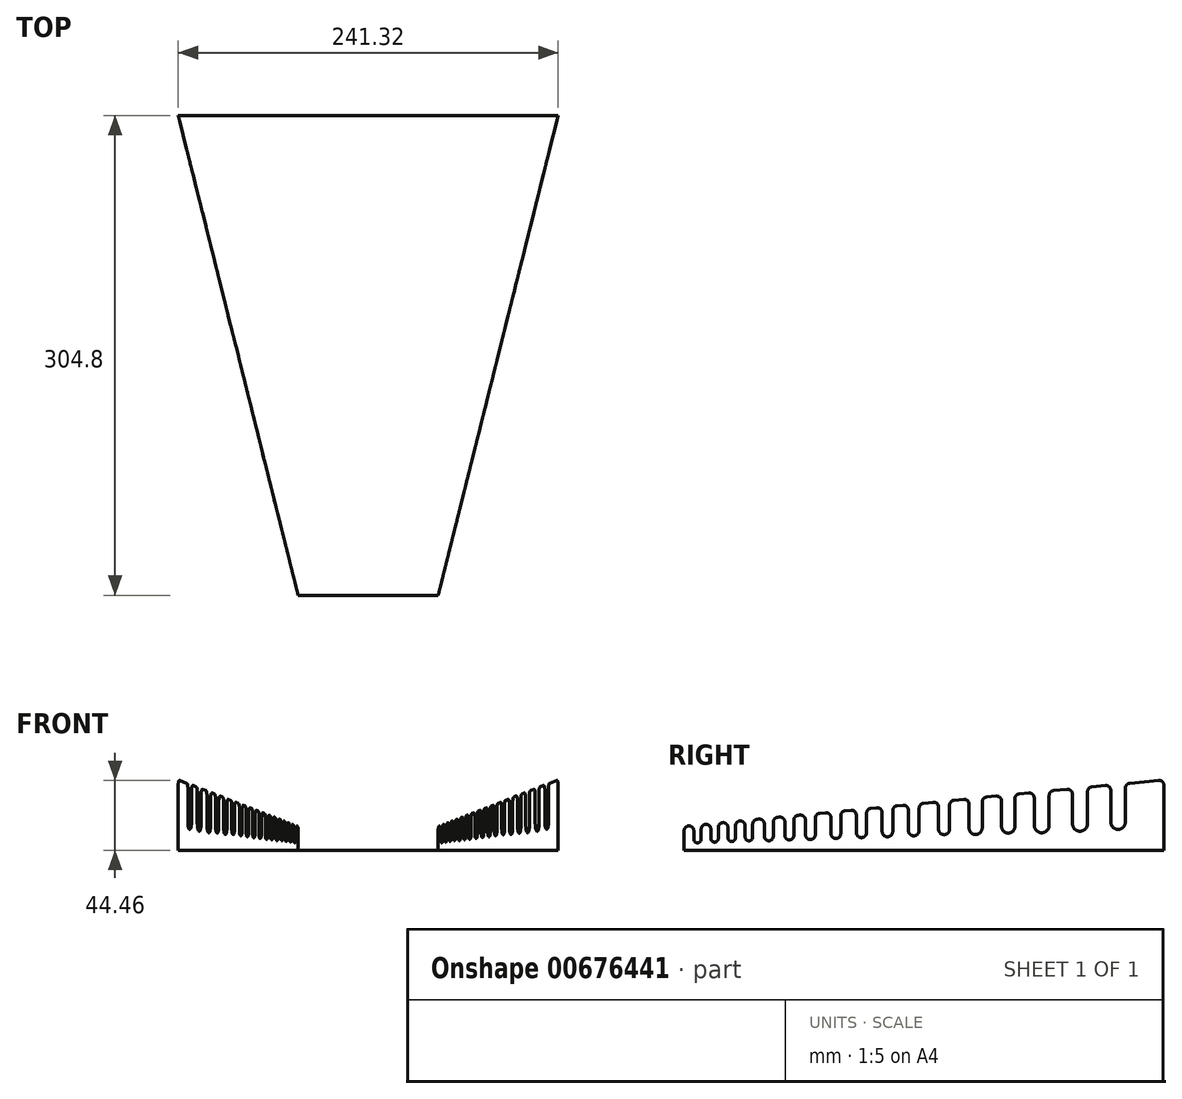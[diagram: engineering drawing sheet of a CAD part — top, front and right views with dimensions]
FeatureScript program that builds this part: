
annotation { "Feature Type Name" : "Feature", "Feature Type Description" : "" }
export const myFeature = defineFeature(function(context is Context, id is Id, definition is map)
    precondition{}
    {
        {
            var Q0;
            Q0=qCreatedBy(makeId("Top.planeOp"),FACE);
            var sketch = newSketch(context, id + "F0", { "sketchPlane" : qUnion([Q0])});
            skLineSegment(sketch, "E0", {"start": v(-44.45, 0) * mm, "end": v(44.45, 0) * mm});
            skLineSegment(sketch, "E1", {"start": v(44.45, 0) * mm, "end": v(120.65, 304.8) * mm});
            skLineSegment(sketch, "E2", {"start": v(120.65, 304.8) * mm, "end": v(-120.65, 304.8) * mm});
            skLineSegment(sketch, "E3", {"start": v(-120.65, 304.8) * mm, "end": v(-44.45, 0) * mm});
            skSolve(sketch);
        }
        {
            var Q0;
            Q0=qSketchRegion(id+"F0",true);
            extrude(context, id + "F1", {"entities" : qUnion([Q0]), "depth" : 3 / 406.4 * mm});
        }
        {
            var Q0;
            Q0=makeQuery(id+"F1.opExtrude","SWEPT_FACE",FACE,{"disambiguationData":[OSD([sQuery(id+"F0.wireOp",EDGE,"E1")])]});
            var sketch = newSketch(context, id + "F2", { "sketchPlane" : qUnion([Q0])});
            skLineSegment(sketch, "E4", {"start": v(10.78, 0) * mm, "end": v(10.78, 12.35) * mm});
            skLineSegment(sketch, "E5", {"start": v(13.66, 15.51) * mm, "end": v(13.66, 15.51) * mm});
            skLineSegment(sketch, "E6", {"start": v(17.13, 12.35) * mm, "end": v(17.13, 7.18) * mm});
            skLineSegment(sketch, "E7", {"start": v(17.13, 7.18) * mm, "end": v(21.96, 7.37) * mm, "construction": true});
            skLineSegment(sketch, "E8", {"start": v(21.96, 7.37) * mm, "end": v(21.96, 13.4) * mm});
            skLineSegment(sketch, "E9", {"start": v(24.83, 16.56) * mm, "end": v(24.83, 16.56) * mm});
            skLineSegment(sketch, "E10", {"start": v(28.3, 13.4) * mm, "end": v(28.3, 7.62) * mm});
            skLineSegment(sketch, "E11", {"start": v(28.3, 7.62) * mm, "end": v(33.13, 7.82) * mm, "construction": true});
            skLineSegment(sketch, "E12", {"start": v(33.13, 7.82) * mm, "end": v(33.13, 14.45) * mm});
            skLineSegment(sketch, "E13", {"start": v(36.01, 17.61) * mm, "end": v(36.01, 17.61) * mm});
            skLineSegment(sketch, "E14", {"start": v(39.48, 14.45) * mm, "end": v(39.48, 8.07) * mm});
            skLineSegment(sketch, "E15", {"start": v(39.48, 8.07) * mm, "end": v(44.38, 8.27) * mm, "construction": true});
            skLineSegment(sketch, "E16", {"start": v(44.38, 8.27) * mm, "end": v(44.38, 15.5) * mm});
            skLineSegment(sketch, "E17", {"start": v(47.26, 18.67) * mm, "end": v(47.26, 18.67) * mm});
            skLineSegment(sketch, "E18", {"start": v(50.73, 15.5) * mm, "end": v(50.73, 8.52) * mm});
            skLineSegment(sketch, "E19", {"start": v(50.73, 8.52) * mm, "end": v(55.69, 8.72) * mm, "construction": true});
            skLineSegment(sketch, "E20", {"start": v(55.69, 8.72) * mm, "end": v(55.69, 16.57) * mm});
            skLineSegment(sketch, "E21", {"start": v(58.57, 19.73) * mm, "end": v(59.84, 19.85) * mm});
            skLineSegment(sketch, "E22", {"start": v(63.3, 16.7) * mm, "end": v(63.3, 9.02) * mm});
            skLineSegment(sketch, "E23", {"start": v(63.3, 9.02) * mm, "end": v(69.15, 9.26) * mm, "construction": true});
            skLineSegment(sketch, "E24", {"start": v(69.15, 9.26) * mm, "end": v(69.15, 17.84) * mm});
            skLineSegment(sketch, "E25", {"start": v(72.03, 21) * mm, "end": v(73.3, 21.12) * mm});
            skLineSegment(sketch, "E26", {"start": v(76.77, 17.96) * mm, "end": v(76.77, 9.56) * mm});
            skLineSegment(sketch, "E27", {"start": v(76.77, 9.56) * mm, "end": v(82.61, 9.8) * mm, "construction": true});
            skLineSegment(sketch, "E28", {"start": v(82.61, 9.8) * mm, "end": v(82.61, 19.1) * mm});
            skLineSegment(sketch, "E29", {"start": v(85.49, 22.26) * mm, "end": v(86.76, 22.38) * mm});
            skLineSegment(sketch, "E30", {"start": v(90.23, 19.22) * mm, "end": v(90.23, 10.1) * mm});
            skLineSegment(sketch, "E31", {"start": v(90.23, 10.1) * mm, "end": v(96.7, 10.36) * mm, "construction": true});
            skLineSegment(sketch, "E32", {"start": v(96.7, 10.36) * mm, "end": v(96.7, 20.43) * mm});
            skLineSegment(sketch, "E33", {"start": v(99.59, 23.59) * mm, "end": v(103.4, 23.95) * mm});
            skLineSegment(sketch, "E34", {"start": v(106.87, 20.79) * mm, "end": v(106.87, 10.77) * mm});
            skLineSegment(sketch, "E35", {"start": v(106.87, 10.77) * mm, "end": v(113.35, 11.02) * mm, "construction": true});
            skLineSegment(sketch, "E36", {"start": v(113.35, 11.02) * mm, "end": v(113.35, 22) * mm});
            skLineSegment(sketch, "E37", {"start": v(116.22, 25.15) * mm, "end": v(120.03, 25.51) * mm});
            skLineSegment(sketch, "E38", {"start": v(123.5, 22.35) * mm, "end": v(123.5, 11.43) * mm});
            skLineSegment(sketch, "E39", {"start": v(123.5, 11.43) * mm, "end": v(130.24, 11.7) * mm, "construction": true});
            skLineSegment(sketch, "E40", {"start": v(130.24, 11.7) * mm, "end": v(130.24, 23.58) * mm});
            skLineSegment(sketch, "E41", {"start": v(133.11, 26.74) * mm, "end": v(136.92, 27.1) * mm});
            skLineSegment(sketch, "E42", {"start": v(140.4, 23.94) * mm, "end": v(140.4, 12.1) * mm});
            skLineSegment(sketch, "E43", {"start": v(140.4, 12.1) * mm, "end": v(147.38, 12.39) * mm, "construction": true});
            skLineSegment(sketch, "E44", {"start": v(147.38, 12.39) * mm, "end": v(147.38, 25.2) * mm});
            skLineSegment(sketch, "E45", {"start": v(150.26, 28.35) * mm, "end": v(154.07, 28.71) * mm});
            skLineSegment(sketch, "E46", {"start": v(157.54, 25.55) * mm, "end": v(157.54, 12.8) * mm});
            skLineSegment(sketch, "E47", {"start": v(157.54, 12.8) * mm, "end": v(164.65, 13.08) * mm, "construction": true});
            skLineSegment(sketch, "E48", {"start": v(164.65, 13.08) * mm, "end": v(164.65, 26.82) * mm});
            skLineSegment(sketch, "E49", {"start": v(167.53, 29.98) * mm, "end": v(173.88, 30.57) * mm});
            skLineSegment(sketch, "E50", {"start": v(177.35, 27.41) * mm, "end": v(177.35, 13.59) * mm});
            skLineSegment(sketch, "E51", {"start": v(177.35, 13.59) * mm, "end": v(184.6, 13.88) * mm, "construction": true});
            skLineSegment(sketch, "E52", {"start": v(184.6, 13.88) * mm, "end": v(184.6, 28.69) * mm});
            skLineSegment(sketch, "E53", {"start": v(187.47, 31.85) * mm, "end": v(193.82, 32.45) * mm});
            skLineSegment(sketch, "E54", {"start": v(197.3, 29.29) * mm, "end": v(197.3, 14.38) * mm});
            skLineSegment(sketch, "E55", {"start": v(197.3, 14.38) * mm, "end": v(205.93, 14.73) * mm, "construction": true});
            skLineSegment(sketch, "E56", {"start": v(205.93, 14.73) * mm, "end": v(205.93, 30.7) * mm});
            skLineSegment(sketch, "E57", {"start": v(208.8, 33.86) * mm, "end": v(215.16, 34.45) * mm});
            skLineSegment(sketch, "E58", {"start": v(218.63, 31.3) * mm, "end": v(218.63, 15.24) * mm});
            skLineSegment(sketch, "E59", {"start": v(218.63, 15.24) * mm, "end": v(227.26, 15.58) * mm, "construction": true});
            skLineSegment(sketch, "E60", {"start": v(227.26, 15.58) * mm, "end": v(227.26, 32.7) * mm});
            skLineSegment(sketch, "E61", {"start": v(230.14, 35.86) * mm, "end": v(236.5, 36.46) * mm});
            skLineSegment(sketch, "E62", {"start": v(239.96, 33.3) * mm, "end": v(239.96, 16.1) * mm});
            skLineSegment(sketch, "E63", {"start": v(239.96, 16.1) * mm, "end": v(249.74, 16.48) * mm, "construction": true});
            skLineSegment(sketch, "E64", {"start": v(249.74, 16.48) * mm, "end": v(249.74, 34.81) * mm});
            skLineSegment(sketch, "E65", {"start": v(252.62, 37.98) * mm, "end": v(261.51, 38.81) * mm});
            skLineSegment(sketch, "E66", {"start": v(264.98, 35.65) * mm, "end": v(264.98, 17.1) * mm});
            skLineSegment(sketch, "E67", {"start": v(264.98, 17.1) * mm, "end": v(274.89, 17.49) * mm, "construction": true});
            skLineSegment(sketch, "E68", {"start": v(274.89, 17.49) * mm, "end": v(274.89, 37.18) * mm});
            skLineSegment(sketch, "E69", {"start": v(277.77, 40.34) * mm, "end": v(286.66, 41.18) * mm});
            skLineSegment(sketch, "E70", {"start": v(290.13, 38.01) * mm, "end": v(290.13, 18.1) * mm});
            skLineSegment(sketch, "E71", {"start": v(290.13, 18.1) * mm, "end": v(299.65, 18.48) * mm, "construction": true});
            skLineSegment(sketch, "E72", {"start": v(299.65, 18.48) * mm, "end": v(299.65, 39.5) * mm});
            skLineSegment(sketch, "E73", {"start": v(265.9, 39.22) * mm, "end": v(265.9, 39.22) * mm});
            skLineSegment(sketch, "E74", {"start": v(324.96, 41.29) * mm, "end": v(324.96, 0) * mm});
            skArc(sketch, "E75", {"start": v(17.13, 7.18) * mm, "mid": v(19.64, 4.76) * mm, "end": v(21.96, 7.37) * mm});
            skArc(sketch, "E76", {"start": v(28.3, 7.62) * mm, "mid": v(30.82, 5.2) * mm, "end": v(33.13, 7.82) * mm});
            skArc(sketch, "E77", {"start": v(39.48, 8.07) * mm, "mid": v(42.04, 5.62) * mm, "end": v(44.38, 8.27) * mm});
            skArc(sketch, "E78", {"start": v(50.73, 8.52) * mm, "mid": v(53.31, 6.04) * mm, "end": v(55.69, 8.72) * mm});
            skArc(sketch, "E79", {"start": v(63.3, 9.02) * mm, "mid": v(66.35, 6.1) * mm, "end": v(69.15, 9.26) * mm});
            skArc(sketch, "E80", {"start": v(76.77, 9.56) * mm, "mid": v(79.81, 6.64) * mm, "end": v(82.61, 9.8) * mm});
            skArc(sketch, "E81", {"start": v(90.23, 10.1) * mm, "mid": v(93.6, 6.86) * mm, "end": v(96.7, 10.36) * mm});
            skArc(sketch, "E82", {"start": v(106.87, 10.77) * mm, "mid": v(110.24, 7.52) * mm, "end": v(113.35, 11.02) * mm});
            skArc(sketch, "E83", {"start": v(123.5, 11.43) * mm, "mid": v(127.01, 8.06) * mm, "end": v(130.24, 11.7) * mm});
            skArc(sketch, "E84", {"start": v(140.4, 12.1) * mm, "mid": v(144.03, 8.61) * mm, "end": v(147.38, 12.39) * mm});
            skArc(sketch, "E85", {"start": v(157.54, 12.8) * mm, "mid": v(161.25, 9.23) * mm, "end": v(164.65, 13.08) * mm});
            skArc(sketch, "E86", {"start": v(177.35, 13.59) * mm, "mid": v(181.12, 9.96) * mm, "end": v(184.6, 13.88) * mm});
            skArc(sketch, "E87", {"start": v(197.3, 14.38) * mm, "mid": v(201.8, 10.06) * mm, "end": v(205.93, 14.73) * mm});
            skArc(sketch, "E88", {"start": v(218.63, 15.24) * mm, "mid": v(223.13, 10.92) * mm, "end": v(227.26, 15.58) * mm});
            skArc(sketch, "E89", {"start": v(239.96, 16.1) * mm, "mid": v(245.06, 11.2) * mm, "end": v(249.74, 16.48) * mm});
            skArc(sketch, "E90", {"start": v(264.98, 17.1) * mm, "mid": v(270.14, 12.13) * mm, "end": v(274.89, 17.49) * mm});
            skArc(sketch, "E91", {"start": v(290.13, 18.1) * mm, "mid": v(295.1, 13.33) * mm, "end": v(299.65, 18.48) * mm});
            skArc(sketch, "E92.filletArc", {"start": v(324.96, 41.29) * mm, "mid": v(323.92, 43.64) * mm, "end": v(321.49, 44.45) * mm});
            skArc(sketch, "E93.filletArc", {"start": v(302.53, 42.67) * mm, "mid": v(300.48, 41.64) * mm, "end": v(299.65, 39.5) * mm});
            skPoint(sketch, "E94.visualSharp", {"position": v(290.13, 41.5) * mm});
            skArc(sketch, "E94.filletArc", {"start": v(290.13, 38.01) * mm, "mid": v(289.1, 40.36) * mm, "end": v(286.66, 41.18) * mm});
            skPoint(sketch, "E95.visualSharp", {"position": v(274.89, 40.07) * mm});
            skArc(sketch, "E95.filletArc", {"start": v(277.77, 40.34) * mm, "mid": v(275.72, 39.32) * mm, "end": v(274.89, 37.18) * mm});
            skPoint(sketch, "E96.visualSharp", {"position": v(264.98, 39.14) * mm});
            skArc(sketch, "E96.filletArc", {"start": v(264.98, 35.65) * mm, "mid": v(263.95, 38) * mm, "end": v(261.51, 38.81) * mm});
            skPoint(sketch, "E97.visualSharp", {"position": v(249.74, 37.7) * mm});
            skArc(sketch, "E97.filletArc", {"start": v(252.62, 37.98) * mm, "mid": v(250.57, 36.95) * mm, "end": v(249.74, 34.81) * mm});
            skPoint(sketch, "E98.visualSharp", {"position": v(239.96, 36.79) * mm});
            skArc(sketch, "E98.filletArc", {"start": v(239.96, 33.3) * mm, "mid": v(238.93, 35.65) * mm, "end": v(236.5, 36.46) * mm});
            skPoint(sketch, "E99.visualSharp", {"position": v(227.26, 35.6) * mm});
            skArc(sketch, "E99.filletArc", {"start": v(230.14, 35.86) * mm, "mid": v(228.1, 34.84) * mm, "end": v(227.26, 32.7) * mm});
            skPoint(sketch, "E100.visualSharp", {"position": v(218.63, 34.78) * mm});
            skArc(sketch, "E100.filletArc", {"start": v(218.63, 31.3) * mm, "mid": v(217.6, 33.64) * mm, "end": v(215.16, 34.45) * mm});
            skPoint(sketch, "E101.visualSharp", {"position": v(205.93, 33.59) * mm});
            skArc(sketch, "E101.filletArc", {"start": v(208.8, 33.86) * mm, "mid": v(206.76, 32.83) * mm, "end": v(205.93, 30.7) * mm});
            skPoint(sketch, "E102.visualSharp", {"position": v(197.3, 32.77) * mm});
            skArc(sketch, "E102.filletArc", {"start": v(197.3, 29.29) * mm, "mid": v(196.26, 31.63) * mm, "end": v(193.82, 32.45) * mm});
            skPoint(sketch, "E103.visualSharp", {"position": v(184.6, 31.58) * mm});
            skArc(sketch, "E103.filletArc", {"start": v(187.47, 31.85) * mm, "mid": v(185.42, 30.83) * mm, "end": v(184.6, 28.69) * mm});
            skPoint(sketch, "E104.visualSharp", {"position": v(177.35, 30.9) * mm});
            skArc(sketch, "E104.filletArc", {"start": v(177.35, 27.41) * mm, "mid": v(176.32, 29.76) * mm, "end": v(173.88, 30.57) * mm});
            skPoint(sketch, "E105.visualSharp", {"position": v(164.65, 29.7) * mm});
            skArc(sketch, "E105.filletArc", {"start": v(167.53, 29.98) * mm, "mid": v(165.48, 28.95) * mm, "end": v(164.65, 26.82) * mm});
            skPoint(sketch, "E106.visualSharp", {"position": v(157.54, 29.04) * mm});
            skArc(sketch, "E106.filletArc", {"start": v(157.54, 25.55) * mm, "mid": v(156.5, 27.9) * mm, "end": v(154.07, 28.71) * mm});
            skPoint(sketch, "E107.visualSharp", {"position": v(147.38, 28.08) * mm});
            skArc(sketch, "E107.filletArc", {"start": v(150.26, 28.35) * mm, "mid": v(148.2, 27.33) * mm, "end": v(147.38, 25.2) * mm});
            skPoint(sketch, "E108.visualSharp", {"position": v(140.4, 27.43) * mm});
            skArc(sketch, "E108.filletArc", {"start": v(140.4, 23.94) * mm, "mid": v(139.36, 26.29) * mm, "end": v(136.92, 27.1) * mm});
            skPoint(sketch, "E109.visualSharp", {"position": v(130.24, 26.47) * mm});
            skArc(sketch, "E109.filletArc", {"start": v(133.11, 26.74) * mm, "mid": v(131.06, 25.72) * mm, "end": v(130.24, 23.58) * mm});
            skPoint(sketch, "E110.visualSharp", {"position": v(123.5, 25.84) * mm});
            skArc(sketch, "E110.filletArc", {"start": v(123.5, 22.35) * mm, "mid": v(122.47, 24.7) * mm, "end": v(120.03, 25.51) * mm});
            skPoint(sketch, "E111.visualSharp", {"position": v(113.35, 24.88) * mm});
            skArc(sketch, "E111.filletArc", {"start": v(116.22, 25.15) * mm, "mid": v(114.17, 24.13) * mm, "end": v(113.35, 22) * mm});
            skPoint(sketch, "E112.visualSharp", {"position": v(106.87, 24.27) * mm});
            skArc(sketch, "E112.filletArc", {"start": v(106.87, 20.79) * mm, "mid": v(105.83, 23.13) * mm, "end": v(103.4, 23.95) * mm});
            skPoint(sketch, "E113.visualSharp", {"position": v(96.7, 23.32) * mm});
            skArc(sketch, "E113.filletArc", {"start": v(99.59, 23.59) * mm, "mid": v(97.54, 22.57) * mm, "end": v(96.7, 20.43) * mm});
            skPoint(sketch, "E114.visualSharp", {"position": v(90.23, 22.7) * mm});
            skArc(sketch, "E114.filletArc", {"start": v(90.23, 19.22) * mm, "mid": v(89.2, 21.57) * mm, "end": v(86.76, 22.38) * mm});
            skPoint(sketch, "E115.visualSharp", {"position": v(82.61, 22) * mm});
            skArc(sketch, "E115.filletArc", {"start": v(85.49, 22.26) * mm, "mid": v(83.44, 21.24) * mm, "end": v(82.61, 19.1) * mm});
            skPoint(sketch, "E116.visualSharp", {"position": v(76.77, 21.44) * mm});
            skArc(sketch, "E116.filletArc", {"start": v(76.77, 17.96) * mm, "mid": v(75.73, 20.3) * mm, "end": v(73.3, 21.12) * mm});
            skPoint(sketch, "E117.visualSharp", {"position": v(69.15, 20.73) * mm});
            skArc(sketch, "E117.filletArc", {"start": v(72.03, 21) * mm, "mid": v(69.98, 19.97) * mm, "end": v(69.15, 17.84) * mm});
            skPoint(sketch, "E118.visualSharp", {"position": v(63.3, 20.18) * mm});
            skArc(sketch, "E118.filletArc", {"start": v(63.3, 16.7) * mm, "mid": v(62.27, 19.04) * mm, "end": v(59.84, 19.85) * mm});
            skPoint(sketch, "E119.visualSharp", {"position": v(55.69, 19.46) * mm});
            skArc(sketch, "E119.filletArc", {"start": v(58.57, 19.73) * mm, "mid": v(56.52, 18.7) * mm, "end": v(55.69, 16.57) * mm});
            skPoint(sketch, "E120.visualSharp", {"position": v(50.73, 19) * mm});
            skArc(sketch, "E120.filletArc", {"start": v(50.73, 15.5) * mm, "mid": v(49.7, 17.86) * mm, "end": v(47.26, 18.67) * mm});
            skPoint(sketch, "E121.visualSharp", {"position": v(44.38, 18.4) * mm});
            skArc(sketch, "E121.filletArc", {"start": v(47.26, 18.67) * mm, "mid": v(45.21, 17.65) * mm, "end": v(44.38, 15.5) * mm});
            skPoint(sketch, "E122.visualSharp", {"position": v(39.48, 17.94) * mm});
            skArc(sketch, "E122.filletArc", {"start": v(39.48, 14.45) * mm, "mid": v(38.45, 16.8) * mm, "end": v(36.01, 17.61) * mm});
            skPoint(sketch, "E123.visualSharp", {"position": v(33.13, 17.34) * mm});
            skArc(sketch, "E123.filletArc", {"start": v(36.01, 17.61) * mm, "mid": v(33.96, 16.59) * mm, "end": v(33.13, 14.45) * mm});
            skPoint(sketch, "E124.visualSharp", {"position": v(28.3, 16.89) * mm});
            skArc(sketch, "E124.filletArc", {"start": v(28.3, 13.4) * mm, "mid": v(27.27, 15.75) * mm, "end": v(24.83, 16.56) * mm});
            skPoint(sketch, "E125.visualSharp", {"position": v(21.96, 16.3) * mm});
            skArc(sketch, "E125.filletArc", {"start": v(24.83, 16.56) * mm, "mid": v(22.78, 15.54) * mm, "end": v(21.96, 13.4) * mm});
            skPoint(sketch, "E126.visualSharp", {"position": v(17.13, 15.84) * mm});
            skArc(sketch, "E126.filletArc", {"start": v(17.13, 12.35) * mm, "mid": v(16.1, 14.7) * mm, "end": v(13.66, 15.51) * mm});
            skPoint(sketch, "E127.visualSharp", {"position": v(10.78, 15.24) * mm});
            skArc(sketch, "E127.filletArc", {"start": v(13.66, 15.51) * mm, "mid": v(11.6, 14.49) * mm, "end": v(10.78, 12.35) * mm});
            skLineSegment(sketch, "E128", {"start": v(10.78, 0) * mm, "end": v(324.96, 0) * mm});
            skLineSegment(sketch, "E129", {"start": v(321.49, 44.45) * mm, "end": v(302.53, 42.67) * mm});
            skSolve(sketch);
        }
        {
            var Q0;
            Q0=qSketchRegion(id+"F2",true);
            extrude(context, id + "F3", {"entities" : qUnion([Q0]), "depth" : 3 / 406.4 * mm});
        }
        {
            var Q0;
            Q0=makeQuery(id+"F3.opExtrude","SWEPT_BODY",BODY,{"disambiguationData":[OSD([sQuery(id+"F2.wireOp",EDGE,"E4"),sQuery(id+"F2.wireOp",EDGE,"E5"),sQuery(id+"F2.wireOp",EDGE,"E6"),sQuery(id+"F2.wireOp",EDGE,"E8"),sQuery(id+"F2.wireOp",EDGE,"E9"),sQuery(id+"F2.wireOp",EDGE,"E10"),sQuery(id+"F2.wireOp",EDGE,"E12"),sQuery(id+"F2.wireOp",EDGE,"E13"),sQuery(id+"F2.wireOp",EDGE,"E14"),sQuery(id+"F2.wireOp",EDGE,"E16"),sQuery(id+"F2.wireOp",EDGE,"E17"),sQuery(id+"F2.wireOp",EDGE,"E18"),sQuery(id+"F2.wireOp",EDGE,"E20"),sQuery(id+"F2.wireOp",EDGE,"E21"),sQuery(id+"F2.wireOp",EDGE,"E22"),sQuery(id+"F2.wireOp",EDGE,"E24"),sQuery(id+"F2.wireOp",EDGE,"E25"),sQuery(id+"F2.wireOp",EDGE,"E26"),sQuery(id+"F2.wireOp",EDGE,"E28"),sQuery(id+"F2.wireOp",EDGE,"E29"),sQuery(id+"F2.wireOp",EDGE,"E30"),sQuery(id+"F2.wireOp",EDGE,"E32"),sQuery(id+"F2.wireOp",EDGE,"E33"),sQuery(id+"F2.wireOp",EDGE,"E34"),sQuery(id+"F2.wireOp",EDGE,"E36"),sQuery(id+"F2.wireOp",EDGE,"E37"),sQuery(id+"F2.wireOp",EDGE,"E38"),sQuery(id+"F2.wireOp",EDGE,"E40"),sQuery(id+"F2.wireOp",EDGE,"E41"),sQuery(id+"F2.wireOp",EDGE,"E42"),sQuery(id+"F2.wireOp",EDGE,"E44"),sQuery(id+"F2.wireOp",EDGE,"E45"),sQuery(id+"F2.wireOp",EDGE,"E46"),sQuery(id+"F2.wireOp",EDGE,"E48"),sQuery(id+"F2.wireOp",EDGE,"E49"),sQuery(id+"F2.wireOp",EDGE,"E50"),sQuery(id+"F2.wireOp",EDGE,"E52"),sQuery(id+"F2.wireOp",EDGE,"E53"),sQuery(id+"F2.wireOp",EDGE,"E54"),sQuery(id+"F2.wireOp",EDGE,"E56"),sQuery(id+"F2.wireOp",EDGE,"E57"),sQuery(id+"F2.wireOp",EDGE,"E58"),sQuery(id+"F2.wireOp",EDGE,"E60"),sQuery(id+"F2.wireOp",EDGE,"E61"),sQuery(id+"F2.wireOp",EDGE,"E62"),sQuery(id+"F2.wireOp",EDGE,"E64"),sQuery(id+"F2.wireOp",EDGE,"E65"),sQuery(id+"F2.wireOp",EDGE,"E66"),sQuery(id+"F2.wireOp",EDGE,"E68"),sQuery(id+"F2.wireOp",EDGE,"E70"),sQuery(id+"F2.wireOp",EDGE,"E72"),sQuery(id+"F2.wireOp",EDGE,"9ihwAVwL-yMMt-xmYE-Td51-ayaX15x94NwS"),sQuery(id+"F2.wireOp",EDGE,"6Wx5teZL-wODt-y5db-ANnT-UPmmfWM3Ukpe"),sQuery(id+"F2.wireOp",EDGE,"E85TSMDE-1efA-kweR-pmmq-KC4Xdjg828U5"),sQuery(id+"F2.wireOp",EDGE,"NmcfjtNE-oIZ5-0b0F-BYqz-Lg2e0aJrtCXq"),sQuery(id+"F2.wireOp",EDGE,"dxBorZXQ-VSEu-lgl5-VqOv-JdW7uacsbKmT"),sQuery(id+"F2.wireOp",EDGE,"7qnZEuvj-AQxg-qu0J-dGde-6bTH4GPdGrSV"),sQuery(id+"F2.wireOp",EDGE,"yVdPXEXH-w7M2-4kCM-5lBI-aBlkXL1ZHiPJ"),sQuery(id+"F2.wireOp",EDGE,"aQqWlaiA-IXy9-PBNe-gHCr-Hn8R57gy5fic"),sQuery(id+"F2.wireOp",EDGE,"6GCAIcDh-OiFF-jA3G-d8kp-Ck2v8U8bEO0u"),sQuery(id+"F2.wireOp",EDGE,"Da3AZwT8-KkLN-pfs7-XyQb-8dlWgiG0dyCa"),sQuery(id+"F2.wireOp",EDGE,"kZRNVZUt-hahL-Bpj9-GCHh-G2hXmQbwK9aH"),sQuery(id+"F2.wireOp",EDGE,"LzEq5xnF-NvSS-PmON-YUBG-ChX3msSRTm2m"),sQuery(id+"F2.wireOp",EDGE,"wfnGJh9B-PpQ6-th6Y-06zF-Opqufyt59sBU"),sQuery(id+"F2.wireOp",EDGE,"fs9keDXd-eg4m-qbRe-etzE-jeHQbsrzH9p6"),sQuery(id+"F2.wireOp",EDGE,"E74"),sQuery(id+"F2.wireOp",EDGE,"E75"),sQuery(id+"F2.wireOp",EDGE,"E76"),sQuery(id+"F2.wireOp",EDGE,"E77"),sQuery(id+"F2.wireOp",EDGE,"E78"),sQuery(id+"F2.wireOp",EDGE,"E79"),sQuery(id+"F2.wireOp",EDGE,"E80"),sQuery(id+"F2.wireOp",EDGE,"E81"),sQuery(id+"F2.wireOp",EDGE,"E82"),sQuery(id+"F2.wireOp",EDGE,"E83"),sQuery(id+"F2.wireOp",EDGE,"E84"),sQuery(id+"F2.wireOp",EDGE,"E85"),sQuery(id+"F2.wireOp",EDGE,"E86"),sQuery(id+"F2.wireOp",EDGE,"E87"),sQuery(id+"F2.wireOp",EDGE,"E88"),sQuery(id+"F2.wireOp",EDGE,"E89"),sQuery(id+"F2.wireOp",EDGE,"E90"),sQuery(id+"F2.wireOp",EDGE,"E91"),sQuery(id+"F2.wireOp",EDGE,"51521edc-c36c-4741-a2c8-e6c89847c520"),sQuery(id+"F2.wireOp",EDGE,"c2937420-2c0e-48e4-a297-3b46329f77ed"),sQuery(id+"F2.wireOp",EDGE,"e09dc18e-cf75-4063-a493-89d788ca84c7"),sQuery(id+"F2.wireOp",EDGE,"7a65d38f-d6da-4d3c-822c-5ff490d6cca7"),sQuery(id+"F2.wireOp",EDGE,"786f9d07-c6b8-49c3-99dd-2390568de801"),sQuery(id+"F2.wireOp",EDGE,"E92.filletArc"),sQuery(id+"F2.wireOp",EDGE,"5ea56c1c-ad5f-49d5-96a2-adc58262b3a1.filletArc"),sQuery(id+"F2.wireOp",EDGE,"0aeb03af-12b2-408e-9093-31f995c1a81d.filletArc"),sQuery(id+"F2.wireOp",EDGE,"8812127d-24f4-4bd0-9dec-8077494d4ccb.filletArc"),sQuery(id+"F2.wireOp",EDGE,"cbbaf091-34e9-40b3-b33f-ebed252aad49.filletArc"),sQuery(id+"F2.wireOp",EDGE,"6c4703d3-6c70-417a-8b8e-03f95a004045.filletArc"),sQuery(id+"F2.wireOp",EDGE,"8acad820-d952-4f21-b7f7-e183264cdb16.filletArc"),sQuery(id+"F2.wireOp",EDGE,"bafa3667-eccb-4ae8-90a9-cd3a36b324d0.filletArc"),sQuery(id+"F2.wireOp",EDGE,"a5abbfff-01b3-455a-8b0d-a460608581f8.filletArc"),sQuery(id+"F2.wireOp",EDGE,"af9c7569-dde1-4ec6-9877-167f455a3e9a.filletArc"),sQuery(id+"F2.wireOp",EDGE,"d1f913c9-b633-4928-9db4-b2b14fc9df0b.filletArc"),sQuery(id+"F2.wireOp",EDGE,"E93.filletArc"),sQuery(id+"F2.wireOp",EDGE,"E94.filletArc"),sQuery(id+"F2.wireOp",EDGE,"E95.filletArc"),sQuery(id+"F2.wireOp",EDGE,"E96.filletArc"),sQuery(id+"F2.wireOp",EDGE,"E97.filletArc"),sQuery(id+"F2.wireOp",EDGE,"E98.filletArc"),sQuery(id+"F2.wireOp",EDGE,"E99.filletArc"),sQuery(id+"F2.wireOp",EDGE,"E100.filletArc"),sQuery(id+"F2.wireOp",EDGE,"E101.filletArc"),sQuery(id+"F2.wireOp",EDGE,"E102.filletArc"),sQuery(id+"F2.wireOp",EDGE,"E103.filletArc"),sQuery(id+"F2.wireOp",EDGE,"E104.filletArc"),sQuery(id+"F2.wireOp",EDGE,"E105.filletArc"),sQuery(id+"F2.wireOp",EDGE,"E106.filletArc"),sQuery(id+"F2.wireOp",EDGE,"E107.filletArc"),sQuery(id+"F2.wireOp",EDGE,"E108.filletArc"),sQuery(id+"F2.wireOp",EDGE,"E109.filletArc"),sQuery(id+"F2.wireOp",EDGE,"E110.filletArc"),sQuery(id+"F2.wireOp",EDGE,"E111.filletArc"),sQuery(id+"F2.wireOp",EDGE,"E112.filletArc"),sQuery(id+"F2.wireOp",EDGE,"E113.filletArc"),sQuery(id+"F2.wireOp",EDGE,"E114.filletArc"),sQuery(id+"F2.wireOp",EDGE,"E115.filletArc"),sQuery(id+"F2.wireOp",EDGE,"E116.filletArc"),sQuery(id+"F2.wireOp",EDGE,"E117.filletArc"),sQuery(id+"F2.wireOp",EDGE,"E118.filletArc"),sQuery(id+"F2.wireOp",EDGE,"E119.filletArc"),sQuery(id+"F2.wireOp",EDGE,"E120.filletArc"),sQuery(id+"F2.wireOp",EDGE,"E121.filletArc"),sQuery(id+"F2.wireOp",EDGE,"E122.filletArc"),sQuery(id+"F2.wireOp",EDGE,"E123.filletArc"),sQuery(id+"F2.wireOp",EDGE,"E124.filletArc"),sQuery(id+"F2.wireOp",EDGE,"E125.filletArc"),sQuery(id+"F2.wireOp",EDGE,"E126.filletArc"),sQuery(id+"F2.wireOp",EDGE,"E127.filletArc"),sQuery(id+"F2.wireOp",EDGE,"E128")])]});
            var Q1;
            Q1=qCreatedBy(makeId("Right.planeOp"),FACE);
            mirror(context, id + "F4", {"operationType" : NewBodyOperationType.ADD, "entities" : qUnion([Q0]), "mirrorPlane" : qUnion([Q1])});
        }
    });
